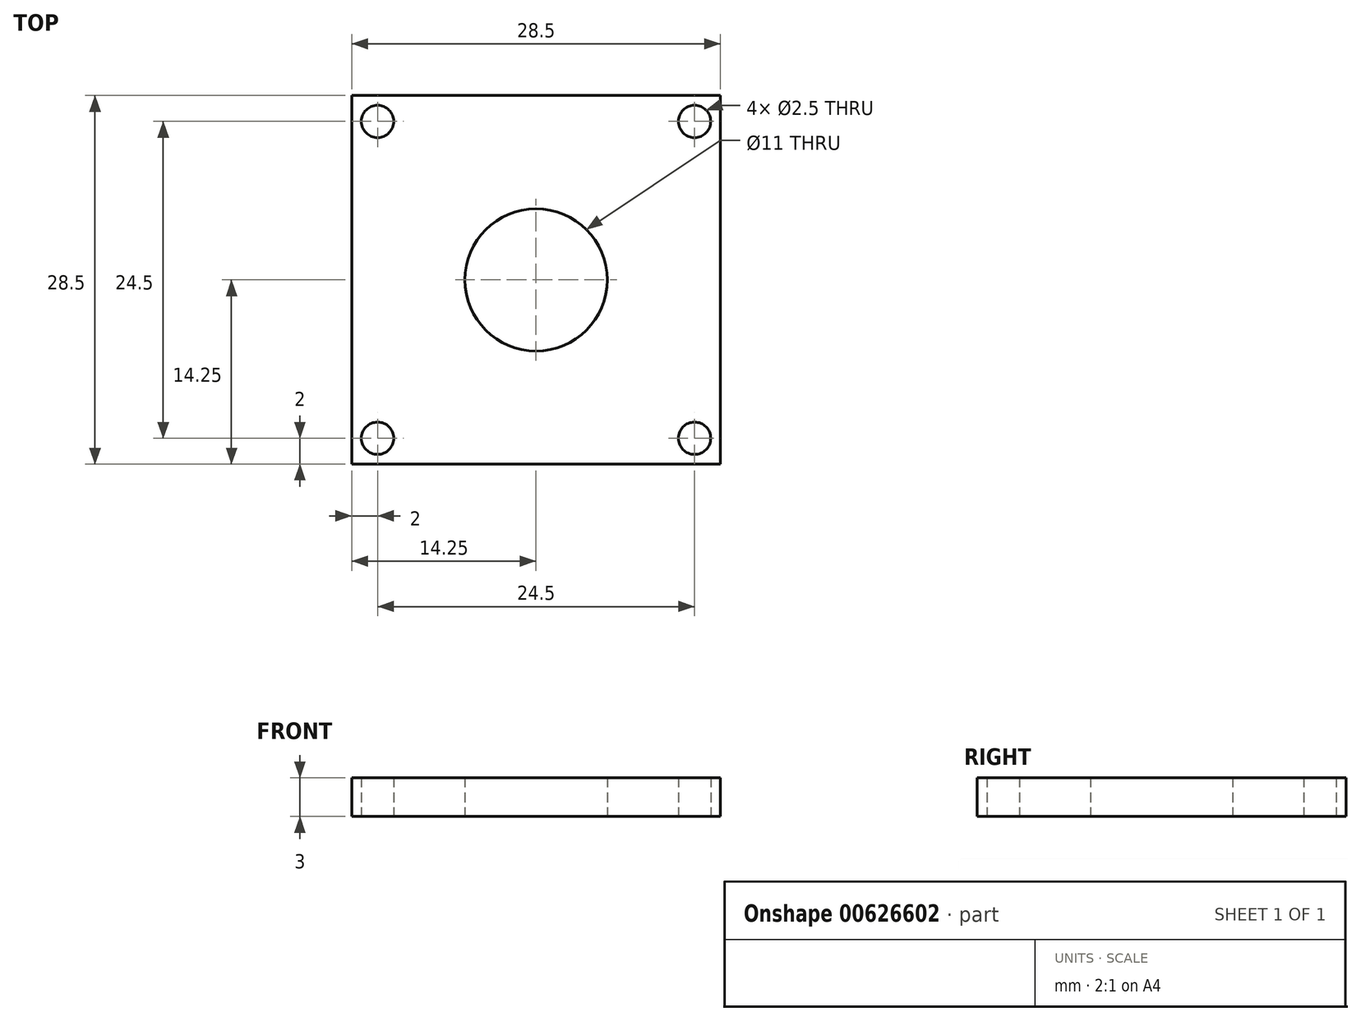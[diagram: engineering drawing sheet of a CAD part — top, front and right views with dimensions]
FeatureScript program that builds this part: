
annotation { "Feature Type Name" : "Feature", "Feature Type Description" : "" }
export const myFeature = defineFeature(function(context is Context, id is Id, definition is map)
    precondition{}
    {
        {
            var Q0;
            Q0=qCreatedBy(makeId("Top.planeOp"),FACE);
            var sketch = newSketch(context, id + "F0", { "sketchPlane" : qUnion([Q0])});
            skLineSegment(sketch, "E0.bottom", {"start": v(14.25, -14.25) * mm, "end": v(-14.25, -14.25) * mm});
            skLineSegment(sketch, "E0.top", {"start": v(14.25, 14.25) * mm, "end": v(-14.25, 14.25) * mm});
            skLineSegment(sketch, "E0.left", {"start": v(14.25, -14.25) * mm, "end": v(14.25, 14.25) * mm});
            skLineSegment(sketch, "E0.right", {"start": v(-14.25, -14.25) * mm, "end": v(-14.25, 14.25) * mm});
            skPoint(sketch, "E0.middle", {"position": v(0, 0) * mm});
            skLineSegment(sketch, "E1.bottom", {"start": v(12.25, 12.25) * mm, "end": v(-12.25, 12.25) * mm, "construction": true});
            skLineSegment(sketch, "E1.top", {"start": v(12.25, -12.25) * mm, "end": v(-12.25, -12.25) * mm, "construction": true});
            skLineSegment(sketch, "E1.left", {"start": v(12.25, 12.25) * mm, "end": v(12.25, -12.25) * mm, "construction": true});
            skLineSegment(sketch, "E1.right", {"start": v(-12.25, 12.25) * mm, "end": v(-12.25, -12.25) * mm, "construction": true});
            skCircle(sketch, "E2", {"center": v(-12.25, 12.25) * mm, "radius": 1.25 * mm});
            skCircle(sketch, "E3", {"center": v(12.25, 12.25) * mm, "radius": 1.25 * mm});
            skCircle(sketch, "E4", {"center": v(-12.25, -12.25) * mm, "radius": 1.25 * mm});
            skCircle(sketch, "E5", {"center": v(12.25, -12.25) * mm, "radius": 1.25 * mm});
            skCircle(sketch, "E6", {"center": v(0, 0) * mm, "radius": 5.5 * mm});
            skSolve(sketch);
        }
        {
            var Q0;
            Q0=makeQuery(id+"F0.imprint","IMPRINT",FACE,{"disambiguationData":[TD([[makeQuery(id+"F0.imprint","IMPRINT",EDGE,{"derivedFrom":sQuery(id+"F0.wireOp",EDGE,"E0.bottom")}),-1.0]])]});
            extrude(context, id + "F1", {"entities" : qUnion([Q0]), "depth" : 3 * mm});
        }
    });
